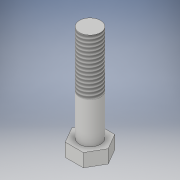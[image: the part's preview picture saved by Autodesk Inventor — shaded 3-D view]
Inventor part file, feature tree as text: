
AUTODESK INVENTOR PART (.ipt)
format: ipt  version: 2018 (Build 220112000, 112)  size: 116,224 bytes
history: native  units: in
note: dims shown in document units (in); Inventor stores cm internally (conversion verified against a paired STEP export)
features: extrude x3, sketch x3, thread x1
ambient origin geometry x8: Origin, YZ Plane, XZ Plane, XY Plane, X Axis, Y Axis, Z Axis, Center Point
bodies: Solid1 (feature_tree)
feature tree (7):
  extrude  "Extrusion1"  Depth=1.068in TaperAngle=0.0deg
  thread  "Thread1"  [1 undecoded]
  extrude  "Extrusion2"  Depth=0.559in
  extrude  "Extrusion3"  Depth=0.235in TaperAngle=0.0deg
  sketch  "Sketch1"  dims[d0=0.375in d1=1.068in d2=0.0in d3=1.0in d4=0.0in]
  sketch  "Sketch2"  dims[d7=0.652in d8=0.0in d9=0.559in]
  sketch  "Sketch3"  dims[d10=0.559in d11=0.235in d12=0.0in]
note: 1 required parameter value undecoded (feature->parameter linkage not recoverable at this tier; creation-order binding heuristic only, values carry confidence <= 0.55)
